# Revit family: Shower-Shower_Column_Kit-KOHLER-ACCLIV-K-33088T-1
name_source: partatom
category: Plumbing Fixtures
units: mm (PartAtom-declared; Revit-internal decimal feet)

## family parameters
Cut with Voids When Loaded = No
Host = Face
Maintain Annotation Orientation = No
OmniClass Number = 23.31.17.00
OmniClass Title = Showers
Part Type = Normal
Room Calculation Point = No
Round Connector Dimension = Use Diameter
Shared = No

## types (6) — shared parameters
ADA Compliant = No
Assembly Code = D2010700
CW Connection = Yes
Cold Water Inlet = Cold Water Inlet
Date Modified = 04/24/2025
Default Elevation = 36"
Drain Included = No
Flow Rate = 0 GPM
HW Connection = Yes
Handle Clearance = 3 5/8"
Height = 60 11/16"
Hot Water Inlet = Hot Water Inlet
Length = 23 5/8"
Manufacturer = Kohler Co.
Master Format 2014 = 22 42 23
Master Format 2014 Name = Residential Showers
Material = Premium Metal Construction
Product Documentation Link = https://files.kohler.com.cn
Product Name = Accliv
Product Page URL = https://www.kohler.com.cn
Spout Reach = 6 11/16"
Tempered Water Inlet = Tempered Water Inlet
URL = http://www.kohler.com.cn
Vent Connection = No
Waste Connection = No
Waste Water Outlet = Waste Water Outlet
WaterSense Certified = No
Width = 5 7/8"

## per-type parameters (varying)
| type | 4 | B4 | Description | Finish | Model | Pressure | Secondary Finish | Type |
| 4, BL-Matte Black | Yes | No | Three water outlet shower column hose connection | Kohler-Metal-BL-Matte_Black | K-33088T-4-BL | 72.50 psi | Plastic-Pantone-PQ-194205-TCX | 2 |
| 4, CP-Polished Chrome | Yes | No | Three water outlet shower column hose connection | Kohler-Metal-CP-Polished_Chrome | K-33088T-4-CP | 72.50 psi | Kohler-Plastic-0-White | 1 |
| 4, BN-Vibrant Brushed Nickel | Yes | No | Three water outlet shower column hose connection | Kohler-Metal-BN-Vibrant_Brushed_Nickel | K-33088T-4-BN | 72.50 psi | Plastic-Pantone-PQ-194205-TCX | 3 |
| 4, AF-Vibrant French Gold | Yes | No | Three water outlet shower column hose connection | Kohler-Metal-AF-Vibrant_French_Gold | K-33088T-4-AF | 72.50 psi | Kohler-Plastic-0-White | 4 |
| B4, BL-Matte Black | No | Yes | Triple Outlet Shower Column – Hose connection | Kohler-Metal-BL-Matte_Black | K-33088T-B4-BL | 0.00 psi | Plastic-Pantone-PQ-194205-TCX | 5 |
| B4, CP-Polished Chrome | No | Yes | Triple Outlet Shower Column – Hose connection | Kohler-Metal-CP-Polished_Chrome | K-33088T-B4-CP | 0.00 psi | Kohler-Plastic-0-White | 6 |

## geometry (parser evidence)
native form markers: Sweep x7
no freeform markers — native parametric forms only
